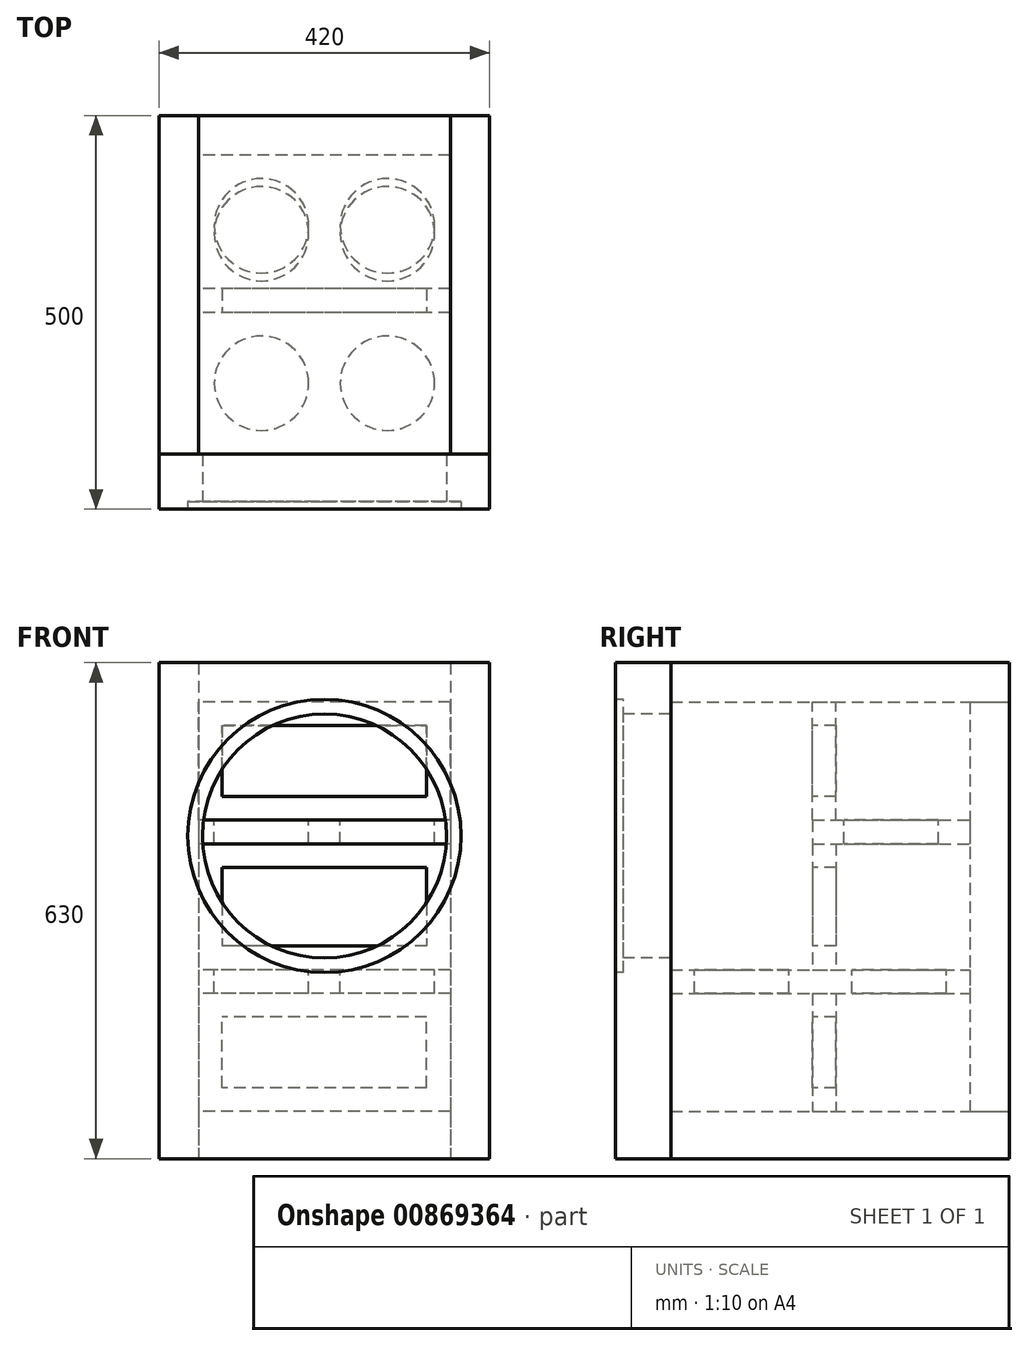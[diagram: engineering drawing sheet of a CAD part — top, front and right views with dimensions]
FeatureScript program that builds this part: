
annotation { "Feature Type Name" : "Feature", "Feature Type Description" : "" }
export const myFeature = defineFeature(function(context is Context, id is Id, definition is map)
    precondition{}
    {
        {
            var Q0;
            Q0=qCreatedBy(makeId("Right.planeOp"),FACE);
            var sketch = newSketch(context, id + "F0", { "sketchPlane" : qUnion([Q0])});
            skLineSegment(sketch, "E0.bottom", {"start": v(0, 0) * mm, "end": v(70, 0) * mm});
            skLineSegment(sketch, "E0.top", {"start": v(0, -630) * mm, "end": v(70, -630) * mm});
            skLineSegment(sketch, "E0.left", {"start": v(0, 0) * mm, "end": v(0, -630) * mm});
            skLineSegment(sketch, "E0.right", {"start": v(70, 0) * mm, "end": v(70, -630) * mm});
            skLineSegment(sketch, "E1.bottom", {"start": v(70, 0) * mm, "end": v(500, 0) * mm});
            skLineSegment(sketch, "E1.top", {"start": v(70, -50) * mm, "end": v(500, -50) * mm});
            skLineSegment(sketch, "E1.left", {"start": v(70, 0) * mm, "end": v(70, -50) * mm});
            skLineSegment(sketch, "E1.right", {"start": v(500, 0) * mm, "end": v(500, -50) * mm});
            skLineSegment(sketch, "E2.bottom", {"start": v(70, -630) * mm, "end": v(500, -630) * mm});
            skLineSegment(sketch, "E2.top", {"start": v(70, -570) * mm, "end": v(500, -570) * mm});
            skLineSegment(sketch, "E2.left", {"start": v(70, -630) * mm, "end": v(70, -570) * mm});
            skLineSegment(sketch, "E2.right", {"start": v(500, -630) * mm, "end": v(500, -570) * mm});
            skLineSegment(sketch, "E3.bottom", {"start": v(500, -50) * mm, "end": v(450, -50) * mm});
            skLineSegment(sketch, "E3.top", {"start": v(500, -570) * mm, "end": v(450, -570) * mm});
            skLineSegment(sketch, "E3.left", {"start": v(500, -50) * mm, "end": v(500, -570) * mm});
            skLineSegment(sketch, "E3.right", {"start": v(450, -50) * mm, "end": v(450, -570) * mm});
            skLineSegment(sketch, "E4.bottom", {"start": v(250, -200) * mm, "end": v(450, -200) * mm});
            skLineSegment(sketch, "E4.top", {"start": v(250, -230) * mm, "end": v(450, -230) * mm});
            skLineSegment(sketch, "E4.left", {"start": v(250, -200) * mm, "end": v(250, -230) * mm});
            skLineSegment(sketch, "E4.right", {"start": v(450, -200) * mm, "end": v(450, -230) * mm});
            skLineSegment(sketch, "E5.bottom", {"start": v(70, -390) * mm, "end": v(450, -390) * mm});
            skLineSegment(sketch, "E5.top", {"start": v(70, -420) * mm, "end": v(450, -420) * mm});
            skLineSegment(sketch, "E5.left", {"start": v(70, -390) * mm, "end": v(70, -420) * mm});
            skLineSegment(sketch, "E5.right", {"start": v(450, -390) * mm, "end": v(450, -420) * mm});
            skLineSegment(sketch, "E6.bottom", {"start": v(250, -200) * mm, "end": v(280, -200) * mm});
            skLineSegment(sketch, "E6.top", {"start": v(250, -50) * mm, "end": v(280, -50) * mm});
            skLineSegment(sketch, "E6.left", {"start": v(250, -200) * mm, "end": v(250, -50) * mm});
            skLineSegment(sketch, "E6.right", {"start": v(280, -200) * mm, "end": v(280, -50) * mm});
            skLineSegment(sketch, "E7.bottom", {"start": v(250, -230) * mm, "end": v(280, -230) * mm});
            skLineSegment(sketch, "E7.top", {"start": v(250, -390) * mm, "end": v(280, -390) * mm});
            skLineSegment(sketch, "E7.left", {"start": v(250, -230) * mm, "end": v(250, -390) * mm});
            skLineSegment(sketch, "E7.right", {"start": v(280, -230) * mm, "end": v(280, -390) * mm});
            skLineSegment(sketch, "E8.bottom", {"start": v(250, -420) * mm, "end": v(280, -420) * mm});
            skLineSegment(sketch, "E8.top", {"start": v(250, -570) * mm, "end": v(280, -570) * mm});
            skLineSegment(sketch, "E8.left", {"start": v(250, -420) * mm, "end": v(250, -570) * mm});
            skLineSegment(sketch, "E8.right", {"start": v(280, -420) * mm, "end": v(280, -570) * mm});
            skSolve(sketch);
        }
        {
            var Q0;
            {var subQ4=sQuery(id+"F0.wireOp",EDGE,"E0.bottom");Q0=makeQuery(id+"F0.imprint","IMPRINT",FACE,{"disambiguationData":[TD([[makeQuery(id+"F0.imprint","IMPRINT",EDGE,{"derivedFrom":subQ4}),-1.0]])]});}
            extrude(context, id + "F1", {"entities" : qUnion([Q0]), "endBound" : BoundingType.SYMMETRIC, "depth" : 420 * mm, "offsetDistance" : 25 * mm});
        }
        {
            var Q0;
            {var subQ3=sQuery(id+"F0.wireOp",EDGE,"E2.bottom");Q0=makeQuery(id+"F0.imprint","IMPRINT",FACE,{"disambiguationData":[TD([[makeQuery(id+"F0.imprint","IMPRINT",EDGE,{"derivedFrom":subQ3}),1.0]])]});}
            extrude(context, id + "F2", {"entities" : qUnion([Q0]), "endBound" : BoundingType.SYMMETRIC, "depth" : 320 * mm, "offsetDistance" : 25 * mm});
        }
        {
            var Q0;
            {var subQ6=sQuery(id+"F0.wireOp",EDGE,"E1.bottom");Q0=makeQuery(id+"F0.imprint","IMPRINT",FACE,{"disambiguationData":[TD([[makeQuery(id+"F0.imprint","IMPRINT",EDGE,{"derivedFrom":subQ6}),-1.0]])]});}
            extrude(context, id + "F3", {"entities" : qUnion([Q0]), "endBound" : BoundingType.SYMMETRIC, "depth" : 320 * mm, "offsetDistance" : 25 * mm});
        }
        {
            var Q0;
            {var subQ0=sQuery(id+"F0.wireOp",EDGE,"E3.left");Q0=makeQuery(id+"F0.imprint","IMPRINT",FACE,{"disambiguationData":[TD([[makeQuery(id+"F0.imprint","IMPRINT",EDGE,{"derivedFrom":subQ0}),-1.0]])]});}
            extrude(context, id + "F4", {"entities" : qUnion([Q0]), "endBound" : BoundingType.SYMMETRIC, "depth" : 320 * mm, "offsetDistance" : 25 * mm});
        }
        {
            var Q0;
            Q0=makeQuery(id+"F1.opExtrude","SWEPT_FACE",FACE,{"disambiguationData":[OSD([sQuery(id+"F0.wireOp",EDGE,"E0.left")])]});
            var sketch = newSketch(context, id + "F5", { "sketchPlane" : qUnion([Q0])});
            skLineSegment(sketch, "E9", {"start": v(0, 0) * mm, "end": v(0, -630) * mm, "construction": true});
            skCircle(sketch, "E10", {"center": v(0, -220) * mm, "radius": 173.5 * mm});
            skCircle(sketch, "E11", {"center": v(0, -220) * mm, "radius": 155 * mm});
            skSolve(sketch);
        }
        {
            var Q0;
            Q0=makeQuery(id+"F5.imprint","IMPRINT",FACE,{"disambiguationData":[TD([[makeQuery(id+"F5.imprint","IMPRINT",EDGE,{"derivedFrom":sQuery(id+"F5.wireOp",EDGE,"E11")}),1.0]])]});
            extrude(context, id + "F6", {"entities" : qUnion([Q0]), "operationType" : NewBodyOperationType.REMOVE, "endBound" : BoundingType.UP_TO_NEXT, "oppositeDirection" : true, "depth" : 25 * mm, "offsetDistance" : 25 * mm});
        }
        {
            var Q0;
            Q0=makeQuery(id+"F5.imprint","IMPRINT",FACE,{"disambiguationData":[TD([[makeQuery(id+"F5.imprint","IMPRINT",EDGE,{"derivedFrom":sQuery(id+"F5.wireOp",EDGE,"E10")}),1.0]])]});
            extrude(context, id + "F7", {"entities" : qUnion([Q0]), "operationType" : NewBodyOperationType.REMOVE, "oppositeDirection" : true, "depth" : 10 * mm, "offsetDistance" : 25 * mm});
        }
        {
            var Q0;
            Q0=makeQuery(id+"F1.opExtrude","SWEPT_FACE",FACE,{"disambiguationData":[OSD([sQuery(id+"F0.wireOp",EDGE,"E0.right")])]});
            var sketch = newSketch(context, id + "F8", { "sketchPlane" : qUnion([Q0])});
            skPoint(sketch, "E12.0", {"position": v(-160, 0) * mm});
            skPoint(sketch, "E12.1", {"position": v(160, 0) * mm});
            skLineSegment(sketch, "E13.bottom", {"start": v(-160, 0) * mm, "end": v(-210, 0) * mm});
            skLineSegment(sketch, "E13.top", {"start": v(-160, -630) * mm, "end": v(-210, -630) * mm});
            skLineSegment(sketch, "E13.left", {"start": v(-160, 0) * mm, "end": v(-160, -630) * mm});
            skLineSegment(sketch, "E13.right", {"start": v(-210, 0) * mm, "end": v(-210, -630) * mm});
            skLineSegment(sketch, "E14.bottom", {"start": v(160, 0) * mm, "end": v(210, 0) * mm});
            skLineSegment(sketch, "E14.top", {"start": v(160, -630) * mm, "end": v(210, -630) * mm});
            skLineSegment(sketch, "E14.left", {"start": v(160, 0) * mm, "end": v(160, -630) * mm});
            skLineSegment(sketch, "E14.right", {"start": v(210, 0) * mm, "end": v(210, -630) * mm});
            skSolve(sketch);
        }
        {
            var Q0;
            Q0=makeQuery(id+"F8.imprint","IMPRINT",FACE,{"disambiguationData":[TD([[makeQuery(id+"F8.imprint","IMPRINT",EDGE,{"derivedFrom":sQuery(id+"F8.wireOp",EDGE,"E13.bottom")}),-1.0]])]});
            var Q1;
            Q1=makeQuery(id+"F4.opExtrude","SWEPT_FACE",FACE,{"disambiguationData":[OSD([sQuery(id+"F0.wireOp",EDGE,"E3.left")])]});
            extrude(context, id + "F9", {"entities" : qUnion([Q0]), "endBound" : BoundingType.UP_TO_SURFACE, "depth" : 25 * mm, "endBoundEntityFace" : qUnion([Q1]), "offsetDistance" : 25 * mm});
        }
        {
            var Q0;
            Q0=makeQuery(id+"F8.imprint","IMPRINT",FACE,{"disambiguationData":[TD([[makeQuery(id+"F8.imprint","IMPRINT",EDGE,{"derivedFrom":sQuery(id+"F8.wireOp",EDGE,"E14.bottom")}),-1.0]])]});
            var Q1;
            Q1=makeQuery(id+"F4.opExtrude","SWEPT_FACE",FACE,{"disambiguationData":[OSD([sQuery(id+"F0.wireOp",EDGE,"E3.left")])]});
            extrude(context, id + "F10", {"entities" : qUnion([Q0]), "endBound" : BoundingType.UP_TO_SURFACE, "depth" : 25 * mm, "endBoundEntityFace" : qUnion([Q1]), "offsetDistance" : 25 * mm});
        }
        {
            var Q0;
            {var subQ2=sQuery(id+"F0.wireOp",EDGE,"E6.left");Q0=makeQuery(id+"F0.imprint","IMPRINT",FACE,{"disambiguationData":[TD([[makeQuery(id+"F0.imprint","IMPRINT",EDGE,{"derivedFrom":subQ2}),-1.0]])]});}
            extrude(context, id + "F11", {"entities" : qUnion([Q0]), "endBound" : BoundingType.SYMMETRIC, "depth" : 320 * mm, "offsetDistance" : 25 * mm});
        }
        {
            var Q0;
            {var subQ6=sQuery(id+"F0.wireOp",EDGE,"E4.left");Q0=makeQuery(id+"F0.imprint","IMPRINT",FACE,{"disambiguationData":[TD([[makeQuery(id+"F0.imprint","IMPRINT",EDGE,{"derivedFrom":subQ6}),1.0]])]});}
            extrude(context, id + "F12", {"entities" : qUnion([Q0]), "endBound" : BoundingType.SYMMETRIC, "depth" : 320 * mm, "offsetDistance" : 25 * mm});
        }
        {
            var Q0;
            {var subQ2=sQuery(id+"F0.wireOp",EDGE,"E7.left");Q0=makeQuery(id+"F0.imprint","IMPRINT",FACE,{"disambiguationData":[TD([[makeQuery(id+"F0.imprint","IMPRINT",EDGE,{"derivedFrom":subQ2}),1.0]])]});}
            extrude(context, id + "F13", {"entities" : qUnion([Q0]), "endBound" : BoundingType.SYMMETRIC, "depth" : 320 * mm, "offsetDistance" : 25 * mm});
        }
        {
            var Q0;
            {var subQ1=sQuery(id+"F0.wireOp",EDGE,"E0.right");var subQ6=sQuery(id+"F0.wireOp",EDGE,"E5.top");var subQ10=makeQuery(id+"F0.imprint","INTERSECT",VERTEX,{"derivedFrom":[subQ1,subQ6]});Q0=makeQuery(id+"F0.imprint","IMPRINT",FACE,{"disambiguationData":[TD([[makeQuery(id+"F0.imprint","IMPRINT",EDGE,{"disambiguationData":[TD([[subQ10,1.0]])],"derivedFrom":subQ1}),1.0]])]});}
            extrude(context, id + "F14", {"entities" : qUnion([Q0]), "endBound" : BoundingType.SYMMETRIC, "depth" : 320 * mm, "offsetDistance" : 25 * mm});
        }
        {
            var Q0;
            {var subQ2=sQuery(id+"F0.wireOp",EDGE,"E8.left");Q0=makeQuery(id+"F0.imprint","IMPRINT",FACE,{"disambiguationData":[TD([[makeQuery(id+"F0.imprint","IMPRINT",EDGE,{"derivedFrom":subQ2}),1.0]])]});}
            extrude(context, id + "F15", {"entities" : qUnion([Q0]), "endBound" : BoundingType.SYMMETRIC, "depth" : 320 * mm, "offsetDistance" : 25 * mm});
        }
        {
            var Q0;
            Q0=makeQuery(id+"F11.opExtrude","SWEPT_FACE",FACE,{"disambiguationData":[OSD([sQuery(id+"F0.wireOp",EDGE,"E6.left")])]});
            var sketch = newSketch(context, id + "F16", { "sketchPlane" : qUnion([Q0])});
            skLineSegment(sketch, "E15.bottom", {"start": v(130, -170) * mm, "end": v(-130, -170) * mm});
            skLineSegment(sketch, "E15.top", {"start": v(130, -80) * mm, "end": v(-130, -80) * mm});
            skLineSegment(sketch, "E15.left", {"start": v(130, -170) * mm, "end": v(130, -80) * mm});
            skLineSegment(sketch, "E15.right", {"start": v(-130, -170) * mm, "end": v(-130, -80) * mm});
            skPoint(sketch, "E15.middle", {"position": v(0, -125) * mm});
            skPoint(sketch, "E15.middle.positionSnap0", {"position": v(160, -125) * mm});
            skPoint(sketch, "E15.middle.positionSnap1", {"position": v(0, -200) * mm});
            skPoint(sketch, "E15.centerSnap0", {"position": v(160, -125) * mm});
            skPoint(sketch, "E15.centerSnap1", {"position": v(0, -200) * mm});
            skSolve(sketch);
        }
        {
            var Q0;
            Q0=makeQuery(id+"F16.imprint","IMPRINT",FACE,{"disambiguationData":[TD([[makeQuery(id+"F16.imprint","IMPRINT",EDGE,{"derivedFrom":sQuery(id+"F16.wireOp",EDGE,"E15.bottom")}),-1.0]])]});
            extrude(context, id + "F17", {"entities" : qUnion([Q0]), "operationType" : NewBodyOperationType.REMOVE, "endBound" : BoundingType.UP_TO_NEXT, "oppositeDirection" : true, "depth" : 25 * mm, "offsetDistance" : 25 * mm});
        }
        {
            var Q0;
            Q0=makeQuery(id+"F13.opExtrude","SWEPT_FACE",FACE,{"disambiguationData":[OSD([sQuery(id+"F0.wireOp",EDGE,"E7.left")])]});
            var sketch = newSketch(context, id + "F18", { "sketchPlane" : qUnion([Q0])});
            skLineSegment(sketch, "E16.bottom", {"start": v(130, -260) * mm, "end": v(-130, -260) * mm});
            skLineSegment(sketch, "E16.top", {"start": v(130, -360) * mm, "end": v(-130, -360) * mm});
            skLineSegment(sketch, "E16.left", {"start": v(130, -260) * mm, "end": v(130, -360) * mm});
            skLineSegment(sketch, "E16.right", {"start": v(-130, -260) * mm, "end": v(-130, -360) * mm});
            skPoint(sketch, "E16.middle", {"position": v(0, -310) * mm});
            skPoint(sketch, "E16.middle.positionSnap0", {"position": v(160, -310) * mm});
            skPoint(sketch, "E16.middle.positionSnap1", {"position": v(0, -230) * mm});
            skPoint(sketch, "E16.centerSnap0", {"position": v(160, -310) * mm});
            skPoint(sketch, "E16.centerSnap1", {"position": v(0, -230) * mm});
            skSolve(sketch);
        }
        {
            var Q0;
            Q0=makeQuery(id+"F18.imprint","IMPRINT",FACE,{"disambiguationData":[TD([[makeQuery(id+"F18.imprint","IMPRINT",EDGE,{"derivedFrom":sQuery(id+"F18.wireOp",EDGE,"E16.bottom")}),1.0]])]});
            extrude(context, id + "F19", {"entities" : qUnion([Q0]), "operationType" : NewBodyOperationType.REMOVE, "endBound" : BoundingType.UP_TO_NEXT, "oppositeDirection" : true, "depth" : 25 * mm, "offsetDistance" : 25 * mm});
        }
        {
            var Q0;
            Q0=makeQuery(id+"F15.opExtrude","SWEPT_FACE",FACE,{"disambiguationData":[OSD([sQuery(id+"F0.wireOp",EDGE,"E8.left")])]});
            var sketch = newSketch(context, id + "F20", { "sketchPlane" : qUnion([Q0])});
            skLineSegment(sketch, "E17.bottom", {"start": v(130, -540) * mm, "end": v(-130, -540) * mm});
            skLineSegment(sketch, "E17.top", {"start": v(130, -450) * mm, "end": v(-130, -450) * mm});
            skLineSegment(sketch, "E17.left", {"start": v(130, -540) * mm, "end": v(130, -450) * mm});
            skLineSegment(sketch, "E17.right", {"start": v(-130, -540) * mm, "end": v(-130, -450) * mm});
            skPoint(sketch, "E17.middle", {"position": v(0, -495) * mm});
            skPoint(sketch, "E17.middle.positionSnap0", {"position": v(160, -495) * mm});
            skPoint(sketch, "E17.middle.positionSnap1", {"position": v(0, -420) * mm});
            skPoint(sketch, "E17.centerSnap0", {"position": v(160, -495) * mm});
            skPoint(sketch, "E17.centerSnap1", {"position": v(0, -420) * mm});
            skSolve(sketch);
        }
        {
            var Q0;
            Q0=makeQuery(id+"F20.imprint","IMPRINT",FACE,{"disambiguationData":[TD([[makeQuery(id+"F20.imprint","IMPRINT",EDGE,{"derivedFrom":sQuery(id+"F20.wireOp",EDGE,"E17.bottom")}),-1.0]])]});
            extrude(context, id + "F21", {"entities" : qUnion([Q0]), "operationType" : NewBodyOperationType.REMOVE, "endBound" : BoundingType.UP_TO_NEXT, "oppositeDirection" : true, "depth" : 25 * mm, "offsetDistance" : 25 * mm});
        }
        {
            var Q0;
            Q0=makeQuery(id+"F12.opExtrude","SWEPT_FACE",FACE,{"disambiguationData":[OSD([sQuery(id+"F0.wireOp",EDGE,"E4.bottom")])]});
            var sketch = newSketch(context, id + "F22", { "sketchPlane" : qUnion([Q0])});
            skLineSegment(sketch, "E18", {"start": v(160, 350) * mm, "end": v(-160, 350) * mm, "construction": true});
            skCircle(sketch, "E19", {"center": v(-80, 350) * mm, "radius": 60 * mm});
            skCircle(sketch, "E20", {"center": v(80, 350) * mm, "radius": 60 * mm});
            skSolve(sketch);
        }
        {
            var Q0;
            Q0=makeQuery(id+"F22.imprint","IMPRINT",FACE,{"disambiguationData":[TD([[makeQuery(id+"F22.imprint","IMPRINT",EDGE,{"derivedFrom":sQuery(id+"F22.wireOp",EDGE,"E19")}),1.0]])]});
            var Q1;
            Q1=makeQuery(id+"F22.imprint","IMPRINT",FACE,{"disambiguationData":[TD([[makeQuery(id+"F22.imprint","IMPRINT",EDGE,{"derivedFrom":sQuery(id+"F22.wireOp",EDGE,"E20")}),1.0]])]});
            extrude(context, id + "F23", {"entities" : qUnion([Q0, Q1]), "operationType" : NewBodyOperationType.REMOVE, "endBound" : BoundingType.UP_TO_NEXT, "oppositeDirection" : true, "depth" : 25 * mm, "offsetDistance" : 25 * mm});
        }
        {
            var Q0;
            Q0=makeQuery(id+"F14.opExtrude","SWEPT_FACE",FACE,{"disambiguationData":[OSD([sQuery(id+"F0.wireOp",EDGE,"E5.bottom")])]});
            var sketch = newSketch(context, id + "F24", { "sketchPlane" : qUnion([Q0])});
            skLineSegment(sketch, "E21", {"start": v(160, 160) * mm, "end": v(-160, 160) * mm, "construction": true});
            skLineSegment(sketch, "E22", {"start": v(160, 360) * mm, "end": v(-160, 360) * mm, "construction": true});
            skCircle(sketch, "E23", {"center": v(-80, 360) * mm, "radius": 60 * mm});
            skCircle(sketch, "E24", {"center": v(80, 360) * mm, "radius": 60 * mm});
            skCircle(sketch, "E25", {"center": v(80, 160) * mm, "radius": 60 * mm});
            skCircle(sketch, "E26", {"center": v(-80, 160) * mm, "radius": 60 * mm});
            skSolve(sketch);
        }
        {
            var Q0;
            Q0=makeQuery(id+"F24.imprint","IMPRINT",FACE,{"disambiguationData":[TD([[makeQuery(id+"F24.imprint","IMPRINT",EDGE,{"derivedFrom":sQuery(id+"F24.wireOp",EDGE,"E23")}),1.0]])]});
            var Q1;
            Q1=makeQuery(id+"F24.imprint","IMPRINT",FACE,{"disambiguationData":[TD([[makeQuery(id+"F24.imprint","IMPRINT",EDGE,{"derivedFrom":sQuery(id+"F24.wireOp",EDGE,"E24")}),1.0]])]});
            var Q2;
            Q2=makeQuery(id+"F24.imprint","IMPRINT",FACE,{"disambiguationData":[TD([[makeQuery(id+"F24.imprint","IMPRINT",EDGE,{"derivedFrom":sQuery(id+"F24.wireOp",EDGE,"E26")}),1.0]])]});
            var Q3;
            Q3=makeQuery(id+"F24.imprint","IMPRINT",FACE,{"disambiguationData":[TD([[makeQuery(id+"F24.imprint","IMPRINT",EDGE,{"derivedFrom":sQuery(id+"F24.wireOp",EDGE,"E25")}),1.0]])]});
            extrude(context, id + "F25", {"entities" : qUnion([Q0, Q1, Q2, Q3]), "operationType" : NewBodyOperationType.REMOVE, "endBound" : BoundingType.UP_TO_NEXT, "oppositeDirection" : true, "depth" : 25 * mm, "offsetDistance" : 25 * mm});
        }
    });
